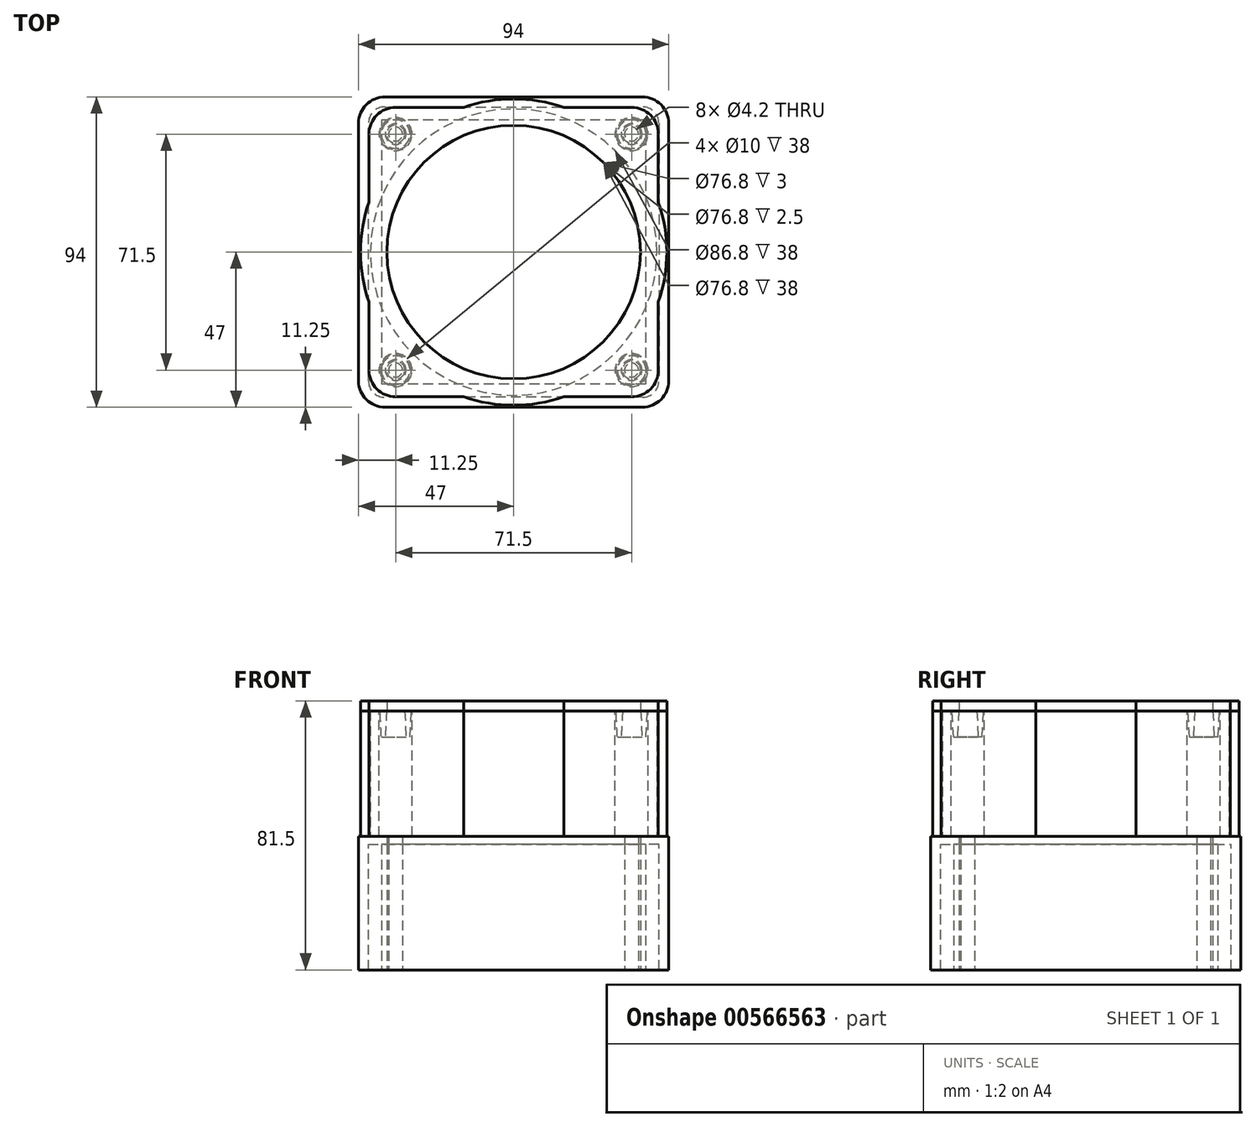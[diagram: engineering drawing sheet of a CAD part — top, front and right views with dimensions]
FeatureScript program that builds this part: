
annotation { "Feature Type Name" : "Feature", "Feature Type Description" : "" }
export const myFeature = defineFeature(function(context is Context, id is Id, definition is map)
    precondition{}
    {
        {
            var Q0;
            Q0=qCreatedBy(makeId("Top.planeOp"),FACE);
            var sketch = newSketch(context, id + "F0", { "sketchPlane" : qUnion([Q0])});
            skLineSegment(sketch, "E0.bottom", {"start": v(35.75, 35.75) * mm, "end": v(-35.75, 35.75) * mm, "construction": true});
            skLineSegment(sketch, "E0.top", {"start": v(35.75, -35.75) * mm, "end": v(-35.75, -35.75) * mm, "construction": true});
            skLineSegment(sketch, "E0.left", {"start": v(35.75, 35.75) * mm, "end": v(35.75, -35.75) * mm, "construction": true});
            skLineSegment(sketch, "E0.right", {"start": v(-35.75, 35.75) * mm, "end": v(-35.75, -35.75) * mm, "construction": true});
            skPoint(sketch, "E0.middle", {"position": v(0, 0) * mm});
            skLineSegment(sketch, "E1.bottom", {"start": v(40, 40) * mm, "end": v(-40, 40) * mm});
            skLineSegment(sketch, "E1.top", {"start": v(40, -40) * mm, "end": v(-40, -40) * mm});
            skLineSegment(sketch, "E1.left", {"start": v(40, 40) * mm, "end": v(40, -40) * mm});
            skLineSegment(sketch, "E1.right", {"start": v(-40, 40) * mm, "end": v(-40, -40) * mm});
            skCircle(sketch, "E2", {"center": v(0, 0) * mm, "radius": 38.4 * mm});
            skLineSegment(sketch, "E3", {"start": v(0, 59.43) * mm, "end": v(0, 0) * mm, "construction": true});
            skLineSegment(sketch, "E4", {"start": v(-63.07, 0) * mm, "end": v(0, 0) * mm, "construction": true});
            skCircle(sketch, "E5", {"center": v(-35.75, 35.75) * mm, "radius": 2.1 * mm});
            skCircle(sketch, "E6.MirrorC", {"center": v(35.75, 35.75) * mm, "radius": 2.1 * mm});
            skCircle(sketch, "E7.MirrorC", {"center": v(35.75, -35.75) * mm, "radius": 2.1 * mm});
            skCircle(sketch, "E8.MirrorC", {"center": v(-35.75, -35.75) * mm, "radius": 2.1 * mm});
            skSolve(sketch);
        }
        {
            var Q0;
            Q0 = qSketchRegion(id + "F0", true);
            extrude(context, id + "F1", {"entities" : qUnion([Q0]), "depth" : 38 * mm, "offsetDistance" : 25 * mm});
        }
        {
            var Q0;
            Q0=makeQuery(id+"F1.opExtrude","CAP_FACE",FACE,{"disambiguationData":[OSD([sQuery(id+"F0.wireOp",EDGE,"E1.bottom"),sQuery(id+"F0.wireOp",EDGE,"E1.top"),sQuery(id+"F0.wireOp",EDGE,"E1.left"),sQuery(id+"F0.wireOp",EDGE,"E1.right"),sQuery(id+"F0.wireOp",EDGE,"E2"),sQuery(id+"F0.wireOp",EDGE,"E5"),sQuery(id+"F0.wireOp",EDGE,"E6.MirrorC"),sQuery(id+"F0.wireOp",EDGE,"E7.MirrorC"),sQuery(id+"F0.wireOp",EDGE,"E8.MirrorC")])],"isStart":false});
            var sketch = newSketch(context, id + "F2", { "sketchPlane" : qUnion([Q0])});
            skCircle(sketch, "E9.0", {"center": v(0, 0) * mm, "radius": 38.4 * mm});
            skCircle(sketch, "E10.0", {"center": v(-35.75, 35.75) * mm, "radius": 2.1 * mm});
            skCircle(sketch, "E11.0", {"center": v(35.75, 35.75) * mm, "radius": 2.1 * mm});
            skCircle(sketch, "E11.1", {"center": v(35.75, -35.75) * mm, "radius": 2.1 * mm});
            skCircle(sketch, "E11.2", {"center": v(-35.75, -35.75) * mm, "radius": 2.1 * mm});
            skLineSegment(sketch, "E12.bottom", {"start": v(47, 47) * mm, "end": v(-47, 47) * mm});
            skLineSegment(sketch, "E12.top", {"start": v(47, -47) * mm, "end": v(-47, -47) * mm});
            skLineSegment(sketch, "E12.left", {"start": v(47, 47) * mm, "end": v(47, -47) * mm});
            skLineSegment(sketch, "E12.right", {"start": v(-47, 47) * mm, "end": v(-47, -47) * mm});
            skSolve(sketch);
        }
        {
            var Q0;
            Q0 = qSketchRegion(id + "F2", true);
            extrude(context, id + "F3", {"entities" : qUnion([Q0]), "depth" : 2.5 * mm, "offsetDistance" : 25 * mm});
        }
        {
            var Q0;
            Q0=makeQuery(id+"F3.opExtrude","CAP_FACE",FACE,{"disambiguationData":[OSD([sQuery(id+"F2.wireOp",EDGE,"E9.0"),sQuery(id+"F2.wireOp",EDGE,"E10.0"),sQuery(id+"F2.wireOp",EDGE,"E11.0"),sQuery(id+"F2.wireOp",EDGE,"E11.1"),sQuery(id+"F2.wireOp",EDGE,"E11.2"),sQuery(id+"F2.wireOp",EDGE,"E12.bottom"),sQuery(id+"F2.wireOp",EDGE,"E12.top"),sQuery(id+"F2.wireOp",EDGE,"E12.left"),sQuery(id+"F2.wireOp",EDGE,"E12.right")])],"isStart":true});
            var sketch = newSketch(context, id + "F4", { "sketchPlane" : qUnion([Q0])});
            skLineSegment(sketch, "E13.0.0", {"start": v(47, 47) * mm, "end": v(-47, 47) * mm});
            skLineSegment(sketch, "E13.0.1", {"start": v(-47, 47) * mm, "end": v(-47, -47) * mm});
            skLineSegment(sketch, "E13.0.2", {"start": v(-47, -47) * mm, "end": v(47, -47) * mm});
            skLineSegment(sketch, "E13.0.3", {"start": v(47, -47) * mm, "end": v(47, 47) * mm});
            skLineSegment(sketch, "E14.0", {"start": v(44, 44) * mm, "end": v(-44, 44) * mm});
            skLineSegment(sketch, "E14.1", {"start": v(44, -44) * mm, "end": v(44, 44) * mm});
            skLineSegment(sketch, "E14.2", {"start": v(-44, -44) * mm, "end": v(44, -44) * mm});
            skLineSegment(sketch, "E14.3", {"start": v(-44, 44) * mm, "end": v(-44, -44) * mm});
            skSolve(sketch);
        }
        {
            var Q0;
            Q0 = qSketchRegion(id + "F4", true);
            var Q1;
            Q1=makeQuery(id+"F1.opExtrude","CAP_FACE",FACE,{"disambiguationData":[OSD([sQuery(id+"F0.wireOp",EDGE,"E1.bottom"),sQuery(id+"F0.wireOp",EDGE,"E1.top"),sQuery(id+"F0.wireOp",EDGE,"E1.left"),sQuery(id+"F0.wireOp",EDGE,"E1.right"),sQuery(id+"F0.wireOp",EDGE,"E2"),sQuery(id+"F0.wireOp",EDGE,"E5"),sQuery(id+"F0.wireOp",EDGE,"E6.MirrorC"),sQuery(id+"F0.wireOp",EDGE,"E7.MirrorC"),sQuery(id+"F0.wireOp",EDGE,"E8.MirrorC")])],"isStart":true});
            extrude(context, id + "F5", {"entities" : qUnion([Q0]), "operationType" : NewBodyOperationType.ADD, "endBound" : BoundingType.UP_TO_SURFACE, "depth" : 25 * mm, "endBoundEntityFace" : qUnion([Q1]), "offsetDistance" : 25 * mm});
        }
        {
            var Q0;
            Q0=makeQuery(id+"F3.opExtrude","CAP_FACE",FACE,{"disambiguationData":[OSD([sQuery(id+"F2.wireOp",EDGE,"E9.0"),sQuery(id+"F2.wireOp",EDGE,"E10.0"),sQuery(id+"F2.wireOp",EDGE,"E11.0"),sQuery(id+"F2.wireOp",EDGE,"E11.1"),sQuery(id+"F2.wireOp",EDGE,"E11.2"),sQuery(id+"F2.wireOp",EDGE,"E12.bottom"),sQuery(id+"F2.wireOp",EDGE,"E12.top"),sQuery(id+"F2.wireOp",EDGE,"E12.left"),sQuery(id+"F2.wireOp",EDGE,"E12.right")])],"isStart":false});
            var sketch = newSketch(context, id + "F6", { "sketchPlane" : qUnion([Q0])});
            skCircle(sketch, "E15", {"center": v(0, 0) * mm, "radius": 43.4 * mm});
            skArc(sketch, "E16", {"start": v(-43.85, 15.17) * mm, "mid": v(-46.4, 0) * mm, "end": v(-43.85, -15.17) * mm});
            skArc(sketch, "E17", {"start": v(-43.85, 35.75) * mm, "mid": v(-41.48, 41.48) * mm, "end": v(-35.75, 43.85) * mm});
            skLineSegment(sketch, "E18", {"start": v(-35.75, 43.85) * mm, "end": v(-15.17, 43.85) * mm});
            skLineSegment(sketch, "E19", {"start": v(-43.85, 35.75) * mm, "end": v(-43.85, 15.17) * mm});
            skLineSegment(sketch, "E20", {"start": v(-41.48, 41.48) * mm, "end": v(0, 0) * mm, "construction": true});
            skLineSegment(sketch, "E21.1.0", {"start": v(-35.75, -43.85) * mm, "end": v(-15.17, -43.85) * mm});
            skArc(sketch, "E21.1.1", {"start": v(-35.75, -43.85) * mm, "mid": v(-41.48, -41.48) * mm, "end": v(-43.85, -35.75) * mm});
            skLineSegment(sketch, "E21.1.2", {"start": v(-43.85, -35.75) * mm, "end": v(-43.85, -15.17) * mm});
            skLineSegment(sketch, "E21.2.0", {"start": v(43.85, -35.75) * mm, "end": v(43.85, -15.17) * mm});
            skArc(sketch, "E21.2.1", {"start": v(43.85, -35.75) * mm, "mid": v(41.48, -41.48) * mm, "end": v(35.75, -43.85) * mm});
            skLineSegment(sketch, "E21.2.2", {"start": v(35.75, -43.85) * mm, "end": v(15.17, -43.85) * mm});
            skLineSegment(sketch, "E21.3.0", {"start": v(35.75, 43.85) * mm, "end": v(15.17, 43.85) * mm});
            skArc(sketch, "E21.3.1", {"start": v(35.75, 43.85) * mm, "mid": v(41.48, 41.48) * mm, "end": v(43.85, 35.75) * mm});
            skLineSegment(sketch, "E21.3.2", {"start": v(43.85, 35.75) * mm, "end": v(43.85, 15.17) * mm});
            skArc(sketch, "E22.trimOffspring", {"start": v(15.17, 43.85) * mm, "mid": v(0, 46.4) * mm, "end": v(-15.17, 43.85) * mm});
            skArc(sketch, "E23.trimOffspring", {"start": v(43.85, -15.17) * mm, "mid": v(46.4, 0) * mm, "end": v(43.85, 15.17) * mm});
            skArc(sketch, "E24.trimOffspring", {"start": v(-15.17, -43.85) * mm, "mid": v(0, -46.4) * mm, "end": v(15.17, -43.85) * mm});
            skSolve(sketch);
        }
        {
            var Q0;
            Q0 = qSketchRegion(id + "F6", true);
            extrude(context, id + "F7", {"entities" : qUnion([Q0]), "operationType" : NewBodyOperationType.ADD, "depth" : 38 * mm, "offsetDistance" : 25 * mm});
        }
        {
            var Q0;
            Q0=makeQuery(id+"F7.opExtrude","CAP_FACE",FACE,{"disambiguationData":[OSD([sQuery(id+"F6.wireOp",EDGE,"E15"),sQuery(id+"F6.wireOp",EDGE,"E16"),sQuery(id+"F6.wireOp",EDGE,"E17"),sQuery(id+"F6.wireOp",EDGE,"E18"),sQuery(id+"F6.wireOp",EDGE,"E19"),sQuery(id+"F6.wireOp",EDGE,"E21.1.0"),sQuery(id+"F6.wireOp",EDGE,"E21.1.1"),sQuery(id+"F6.wireOp",EDGE,"E21.1.2"),sQuery(id+"F6.wireOp",EDGE,"E21.2.0"),sQuery(id+"F6.wireOp",EDGE,"E21.2.1"),sQuery(id+"F6.wireOp",EDGE,"E21.2.2"),sQuery(id+"F6.wireOp",EDGE,"E21.3.0"),sQuery(id+"F6.wireOp",EDGE,"E21.3.1"),sQuery(id+"F6.wireOp",EDGE,"E21.3.2"),sQuery(id+"F6.wireOp",EDGE,"E22.trimOffspring"),sQuery(id+"F6.wireOp",EDGE,"E23.trimOffspring"),sQuery(id+"F6.wireOp",EDGE,"E24.trimOffspring")])],"isStart":false});
            var sketch = newSketch(context, id + "F8", { "sketchPlane" : qUnion([Q0])});
            skCircle(sketch, "E25", {"center": v(-35.75, 35.75) * mm, "radius": 5 * mm});
            skCircle(sketch, "E26.1.0", {"center": v(-35.75, -35.75) * mm, "radius": 5 * mm});
            skCircle(sketch, "E26.2.0", {"center": v(35.75, -35.75) * mm, "radius": 5 * mm});
            skCircle(sketch, "E26.3.0", {"center": v(35.75, 35.75) * mm, "radius": 5 * mm});
            skPoint(sketch, "E26.center", {"position": v(0, 0) * mm});
            skSolve(sketch);
        }
        {
            var Q0;
            Q0 = qSketchRegion(id + "F8", true);
            var Q1;
            {var subQ0=sQuery(id+"F2.wireOp",EDGE,"E12.right");var subQ1=sQuery(id+"F2.wireOp",EDGE,"E12.bottom");var subQ2=sQuery(id+"F2.wireOp",EDGE,"E12.top");var subQ3=sQuery(id+"F2.wireOp",EDGE,"E12.left");Q1=makeQuery(id+"F7.boolean.opBoolean","SPLIT",FACE,{"disambiguationData":[TD([makeQuery(id+"F3.opExtrude","SWEPT_FACE",FACE,{"disambiguationData":[OSD([subQ1])]})])],"derivedFrom":makeQuery(id+"F3.opExtrude","CAP_FACE",FACE,{"disambiguationData":[OSD([sQuery(id+"F2.wireOp",EDGE,"E9.0"),sQuery(id+"F2.wireOp",EDGE,"E10.0"),sQuery(id+"F2.wireOp",EDGE,"E11.0"),sQuery(id+"F2.wireOp",EDGE,"E11.1"),sQuery(id+"F2.wireOp",EDGE,"E11.2"),subQ1,subQ2,subQ3,subQ0])],"isStart":false})});}
            extrude(context, id + "F9", {"entities" : qUnion([Q0]), "operationType" : NewBodyOperationType.REMOVE, "endBound" : BoundingType.UP_TO_SURFACE, "oppositeDirection" : true, "depth" : 25 * mm, "endBoundEntityFace" : qUnion([Q1]), "offsetDistance" : 25 * mm});
        }
        {
            var Q0;
            Q0=makeQuery(id+"F5.opExtrude","SWEPT_EDGE",EDGE,{"disambiguationData":[OSD([sQuery(id+"F4.wireOp",EDGE,"E14.0"),sQuery(id+"F4.wireOp",EDGE,"E14.1")])]});
            var Q1;
            Q1=makeQuery(id+"F5.opExtrude","SWEPT_EDGE",EDGE,{"disambiguationData":[OSD([sQuery(id+"F4.wireOp",EDGE,"E14.0"),sQuery(id+"F4.wireOp",EDGE,"E14.3")])]});
            var Q2;
            Q2=makeQuery(id+"F5.opExtrude","SWEPT_EDGE",EDGE,{"disambiguationData":[OSD([sQuery(id+"F4.wireOp",EDGE,"E14.2"),sQuery(id+"F4.wireOp",EDGE,"E14.3")])]});
            var Q3;
            Q3=makeQuery(id+"F5.opExtrude","SWEPT_EDGE",EDGE,{"disambiguationData":[OSD([sQuery(id+"F4.wireOp",EDGE,"E14.1"),sQuery(id+"F4.wireOp",EDGE,"E14.2")])]});
            fillet(context, id + "F10", {"entities" : qUnion([Q0, Q1, Q2, Q3]), "radius" : 5 * mm, "tangentPropagation" : true, "allowEdgeOverflow" : false});
        }
        {
            var Q0;
            Q0=makeQuery(id+"F5.boolean.opBoolean","MERGE",EDGE,{"derivedFrom":[makeQuery(id+"F3.opExtrude","SWEPT_EDGE",EDGE,{"disambiguationData":[OSD([sQuery(id+"F2.wireOp",EDGE,"E12.top"),sQuery(id+"F2.wireOp",EDGE,"E12.right")])]}),makeQuery(id+"F5.opExtrude","SWEPT_EDGE",EDGE,{"disambiguationData":[OSD([sQuery(id+"F4.wireOp",EDGE,"E13.0.0"),sQuery(id+"F4.wireOp",EDGE,"E13.0.1")])]})]});
            var Q1;
            Q1=makeQuery(id+"F5.boolean.opBoolean","MERGE",EDGE,{"derivedFrom":[makeQuery(id+"F3.opExtrude","SWEPT_EDGE",EDGE,{"disambiguationData":[OSD([sQuery(id+"F2.wireOp",EDGE,"E12.top"),sQuery(id+"F2.wireOp",EDGE,"E12.left")])]}),makeQuery(id+"F5.opExtrude","SWEPT_EDGE",EDGE,{"disambiguationData":[OSD([sQuery(id+"F4.wireOp",EDGE,"E13.0.0"),sQuery(id+"F4.wireOp",EDGE,"E13.0.3")])]})]});
            var Q2;
            Q2=makeQuery(id+"F5.boolean.opBoolean","MERGE",EDGE,{"derivedFrom":[makeQuery(id+"F3.opExtrude","SWEPT_EDGE",EDGE,{"disambiguationData":[OSD([sQuery(id+"F2.wireOp",EDGE,"E12.bottom"),sQuery(id+"F2.wireOp",EDGE,"E12.right")])]}),makeQuery(id+"F5.opExtrude","SWEPT_EDGE",EDGE,{"disambiguationData":[OSD([sQuery(id+"F4.wireOp",EDGE,"E13.0.1"),sQuery(id+"F4.wireOp",EDGE,"E13.0.2")])]})]});
            var Q3;
            Q3=makeQuery(id+"F5.boolean.opBoolean","MERGE",EDGE,{"derivedFrom":[makeQuery(id+"F3.opExtrude","SWEPT_EDGE",EDGE,{"disambiguationData":[OSD([sQuery(id+"F2.wireOp",EDGE,"E12.bottom"),sQuery(id+"F2.wireOp",EDGE,"E12.left")])]}),makeQuery(id+"F5.opExtrude","SWEPT_EDGE",EDGE,{"disambiguationData":[OSD([sQuery(id+"F4.wireOp",EDGE,"E13.0.2"),sQuery(id+"F4.wireOp",EDGE,"E13.0.3")])]})]});
            fillet(context, id + "F11", {"entities" : qUnion([Q0, Q1, Q2, Q3]), "radius" : 8 * mm, "tangentPropagation" : true, "allowEdgeOverflow" : false});
        }
        {
            var Q0;
            Q0=makeQuery(id+"F7.opExtrude","CAP_FACE",FACE,{"disambiguationData":[OSD([sQuery(id+"F6.wireOp",EDGE,"E15"),sQuery(id+"F6.wireOp",EDGE,"E16"),sQuery(id+"F6.wireOp",EDGE,"E17"),sQuery(id+"F6.wireOp",EDGE,"E18"),sQuery(id+"F6.wireOp",EDGE,"E19"),sQuery(id+"F6.wireOp",EDGE,"E21.1.0"),sQuery(id+"F6.wireOp",EDGE,"E21.1.1"),sQuery(id+"F6.wireOp",EDGE,"E21.1.2"),sQuery(id+"F6.wireOp",EDGE,"E21.2.0"),sQuery(id+"F6.wireOp",EDGE,"E21.2.1"),sQuery(id+"F6.wireOp",EDGE,"E21.2.2"),sQuery(id+"F6.wireOp",EDGE,"E21.3.0"),sQuery(id+"F6.wireOp",EDGE,"E21.3.1"),sQuery(id+"F6.wireOp",EDGE,"E21.3.2"),sQuery(id+"F6.wireOp",EDGE,"E22.trimOffspring"),sQuery(id+"F6.wireOp",EDGE,"E23.trimOffspring"),sQuery(id+"F6.wireOp",EDGE,"E24.trimOffspring")])],"isStart":false});
            var sketch = newSketch(context, id + "F12", { "sketchPlane" : qUnion([Q0])});
            skCircle(sketch, "E27.0", {"center": v(0, 0) * mm, "radius": 38.4 * mm});
            skLineSegment(sketch, "E28.0.0", {"start": v(15.17, -43.85) * mm, "end": v(35.75, -43.85) * mm});
            skArc(sketch, "E28.0.1", {"start": v(35.75, -43.85) * mm, "mid": v(41.48, -41.48) * mm, "end": v(43.85, -35.75) * mm});
            skLineSegment(sketch, "E28.0.2", {"start": v(43.85, -35.75) * mm, "end": v(43.85, -15.17) * mm});
            skArc(sketch, "E28.0.3", {"start": v(43.85, -15.17) * mm, "mid": v(46.4, 0) * mm, "end": v(43.85, 15.17) * mm});
            skLineSegment(sketch, "E28.0.4", {"start": v(43.85, 15.17) * mm, "end": v(43.85, 35.75) * mm});
            skArc(sketch, "E28.0.5", {"start": v(43.85, 35.75) * mm, "mid": v(41.48, 41.48) * mm, "end": v(35.75, 43.85) * mm});
            skLineSegment(sketch, "E28.0.6", {"start": v(35.75, 43.85) * mm, "end": v(15.17, 43.85) * mm});
            skArc(sketch, "E28.0.7", {"start": v(15.17, 43.85) * mm, "mid": v(0, 46.4) * mm, "end": v(-15.17, 43.85) * mm});
            skLineSegment(sketch, "E28.0.8", {"start": v(-15.17, 43.85) * mm, "end": v(-35.75, 43.85) * mm});
            skArc(sketch, "E28.0.9", {"start": v(-35.75, 43.85) * mm, "mid": v(-41.48, 41.48) * mm, "end": v(-43.85, 35.75) * mm});
            skLineSegment(sketch, "E28.0.10", {"start": v(-43.85, 35.75) * mm, "end": v(-43.85, 15.17) * mm});
            skArc(sketch, "E28.0.11", {"start": v(-43.85, 15.17) * mm, "mid": v(-46.4, 0) * mm, "end": v(-43.85, -15.17) * mm});
            skLineSegment(sketch, "E28.0.12", {"start": v(-43.85, -15.17) * mm, "end": v(-43.85, -35.75) * mm});
            skArc(sketch, "E28.0.13", {"start": v(-43.85, -35.75) * mm, "mid": v(-41.48, -41.48) * mm, "end": v(-35.75, -43.85) * mm});
            skLineSegment(sketch, "E28.0.14", {"start": v(-35.75, -43.85) * mm, "end": v(-15.17, -43.85) * mm});
            skArc(sketch, "E28.0.15", {"start": v(-15.17, -43.85) * mm, "mid": v(0, -46.4) * mm, "end": v(15.17, -43.85) * mm});
            skSolve(sketch);
        }
        {
            var Q0;
            Q0 = qSketchRegion(id + "F12", true);
            extrude(context, id + "F13", {"entities" : qUnion([Q0]), "depth" : 3 * mm, "offsetDistance" : 25 * mm});
        }
        {
            var Q0;
            Q0=makeQuery(id+"F13.opExtrude","CAP_FACE",FACE,{"disambiguationData":[OSD([sQuery(id+"F12.wireOp",EDGE,"E27.0"),sQuery(id+"F12.wireOp",EDGE,"E28.0.0"),sQuery(id+"F12.wireOp",EDGE,"E28.0.1"),sQuery(id+"F12.wireOp",EDGE,"E28.0.2"),sQuery(id+"F12.wireOp",EDGE,"E28.0.3"),sQuery(id+"F12.wireOp",EDGE,"E28.0.4"),sQuery(id+"F12.wireOp",EDGE,"E28.0.5"),sQuery(id+"F12.wireOp",EDGE,"E28.0.6"),sQuery(id+"F12.wireOp",EDGE,"E28.0.7"),sQuery(id+"F12.wireOp",EDGE,"E28.0.8"),sQuery(id+"F12.wireOp",EDGE,"E28.0.9"),sQuery(id+"F12.wireOp",EDGE,"E28.0.10"),sQuery(id+"F12.wireOp",EDGE,"E28.0.11"),sQuery(id+"F12.wireOp",EDGE,"E28.0.12"),sQuery(id+"F12.wireOp",EDGE,"E28.0.13"),sQuery(id+"F12.wireOp",EDGE,"E28.0.14"),sQuery(id+"F12.wireOp",EDGE,"E28.0.15")])],"isStart":true});
            var sketch = newSketch(context, id + "F14", { "sketchPlane" : qUnion([Q0])});
            skCircle(sketch, "E29", {"center": v(-35.75, -35.75) * mm, "radius": 4.75 * mm});
            skCircle(sketch, "E30", {"center": v(-35.75, -35.75) * mm, "radius": 2.75 * mm});
            skCircle(sketch, "E31.1.0", {"center": v(35.75, -35.75) * mm, "radius": 4.75 * mm});
            skCircle(sketch, "E31.1.1", {"center": v(35.75, -35.75) * mm, "radius": 2.75 * mm});
            skCircle(sketch, "E31.2.0", {"center": v(35.75, 35.75) * mm, "radius": 4.75 * mm});
            skCircle(sketch, "E31.2.1", {"center": v(35.75, 35.75) * mm, "radius": 2.75 * mm});
            skCircle(sketch, "E31.3.0", {"center": v(-35.75, 35.75) * mm, "radius": 4.75 * mm});
            skCircle(sketch, "E31.3.1", {"center": v(-35.75, 35.75) * mm, "radius": 2.75 * mm});
            skPoint(sketch, "E31.center", {"position": v(0, 0) * mm});
            skSolve(sketch);
        }
        {
            var Q0;
            Q0 = qSketchRegion(id + "F14", true);
            extrude(context, id + "F15", {"entities" : qUnion([Q0]), "operationType" : NewBodyOperationType.ADD, "depth" : 8 * mm, "offsetDistance" : 25 * mm, "hasDraft" : true, "draftAngle" : 3 * degree, "draftPullDirection" : true});
        }
    });
